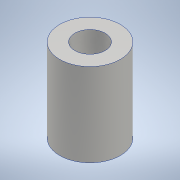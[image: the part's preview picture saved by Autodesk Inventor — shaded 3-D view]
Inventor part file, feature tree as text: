
AUTODESK INVENTOR PART (.ipt)
format: ipt  version: 2020.2 (Build 242310000, 310)  size: 102,400 bytes
history: native  units: mm
features: other x1, extrude x1, sketch x1
ambient origin geometry x8: Origin, YZ Plane, XZ Plane, XY Plane, X Axis, Y Axis, Z Axis, Center Point
bodies: Body1 (feature_tree)
feature tree (3):
  other  "ソリッド1"
  extrude  "押し出し1"  Depth=4.0mm
  sketch  "スケッチ1"
